# Revit family: Haworth_JiveTable_RoundBases
name_source: partatom
category: Furniture Systems
revit_build: Autodesk Revit 2018 (Build: 20170223_1515(x64)
units: mm (PartAtom-declared; Revit-internal decimal feet)

## family parameters
Always vertical = Yes
Cut with Voids When Loaded = No
OmniClass Number = 23.40.70.14.64.21
OmniClass Title = Systems Furniture
Part Type = Normal
Room Calculation Point = No
Round Connector Dimension = Use Diameter
Shared = No
Work Plane-Based = No

## types (33) — shared parameters
Assembly Code = E2020200
Custom Size = No
Manufacturer = Haworth, Inc.
Max. Depth Width = 30"
Max. Height = 42"
Min. Depth Width = 12"
Min. Height = 16"
Model = Haworth Jive
Revision Number = 0
Size = Verify Final Dim. w/ Haworth
Standard Depth Width = 24, 30, 36, 42, 48, 54, 60in.
Standard Heights = 16, 20, 29, 36, 42 in.
Table Thickness = 1 3/16"
URL = https://www.haworth.com
URL - Product = https://www.haworth.com
Warranty = http://www.haworth.com

## per-type parameters (varying)
| type | 4 6 8 Column | 4 Column | 4 Column 48d 48w | 4 Column Leg Distance | Actual Casters | Actual Depth | Actual Glides | Actual Height | Actual Table Depth | Bridge Base 48d 48w only | Casters | DW | Depth | Description | Glides | Height | Leg Height | X Base | X Base 2 3 Column | X Base 48d 48w only | X Base at 48d 48w |
| 30d 30w 29h - X Base - With Casters | No | No | No | 14" | Yes | 15" | No | 29" | 30" | No | Yes | 15" | 30" | Haworth Jive Table Round Bases - 30d 30w 29h - X Base - With Casters | No | 29" | 27 13/16" | Yes | Yes | Yes | No |
| 36d 36w 29h - X Base - With Casters | No | No | No | 14" | Yes | 18" | No | 29" | 36" | No | Yes | 18" | 36" | Haworth Jive Table Round Bases - 36d 36w 29h - X Base - With Casters | No | 29" | 27 13/16" | Yes | Yes | Yes | No |
| 42d 42w 29h - X Base - With Casters | No | No | No | 14" | Yes | 21" | No | 29" | 42" | No | Yes | 21" | 42" | Haworth Jive Table Round Bases - 42d 42w 29h - X Base - With Casters | No | 29" | 27 13/16" | Yes | Yes | Yes | No |
| 48d 48w 29h - X Base - With Casters | No | No | No | 14" | Yes | 24" | No | 29" | 48" | No | Yes | 24" | 48" | Haworth Jive Table Round Bases - 48d 48w 29h - X Base - With Casters | No | 29" | 27 13/16" | Yes | Yes | Yes | Yes |
| 30d 30w 42h - X Base - With Casters | No | No | No | 14" | Yes | 15" | No | 42" | 30" | No | Yes | 15" | 30" | Haworth Jive Table Round Bases - 30d 30w 42h - X Base - With Casters | No | 42" | 40 13/16" | Yes | Yes | Yes | No |
| 36d 36w 42h - X Base - With Casters | No | No | No | 14" | Yes | 18" | No | 42" | 36" | No | Yes | 18" | 36" | Haworth Jive Table Round Bases - 36d 36w 42h - X Base - With Casters | No | 42" | 40 13/16" | Yes | Yes | Yes | No |
| 42d 42w 42h - X Base - With Casters | No | No | No | 14" | Yes | 21" | No | 42" | 42" | No | Yes | 21" | 42" | Haworth Jive Table Round Bases - 42d 42w 42h - X Base - With Casters | No | 42" | 40 13/16" | Yes | Yes | Yes | No |
| 24d 24w 16h - X Base - With Glides | No | No | No | 14" | No | 12" | Yes | 16" | 24" | No | No | 12" | 24" | Haworth Jive Table Round Bases - 24d 24w 16h - X Base - With Glides | Yes | 16" | 14 13/16" | Yes | Yes | Yes | No |
| 30d 30w 16h - X Base - With Glides | No | No | No | 14" | No | 15" | Yes | 16" | 30" | No | No | 15" | 30" | Haworth Jive Table Round Bases - 30d 30w 16h - X Base - With Glides | Yes | 16" | 14 13/16" | Yes | Yes | Yes | No |
| 36d 36w 16h - X Base - With Glides | No | No | No | 14" | No | 18" | Yes | 16" | 36" | No | No | 18" | 36" | Haworth Jive Table Round Bases - 36d 36w 16h - X Base - With Glides | Yes | 16" | 14 13/16" | Yes | Yes | Yes | No |
| 42d 42w 16h - X Base - With Glides | No | No | No | 14" | No | 21" | Yes | 16" | 42" | No | No | 21" | 42" | Haworth Jive Table Round Bases - 42d 42w 16h - X Base - With Glides | Yes | 16" | 14 13/16" | Yes | Yes | Yes | No |
| 48d 48w 16h - X Base - With Glides | No | No | No | 14" | No | 24" | Yes | 16" | 48" | No | No | 24" | 48" | Haworth Jive Table Round Bases - 48d 48w 16h - X Base - With Glides | Yes | 16" | 14 13/16" | Yes | Yes | Yes | Yes |
| 24d 24w 20h - X Base - With Glides | No | No | No | 14" | No | 12" | Yes | 20" | 24" | No | No | 12" | 24" | Haworth Jive Table Round Bases - 24d 24w 20h - X Base - With Glides | Yes | 20" | 18 13/16" | Yes | Yes | Yes | No |
| 30d 30w 20h - X Base - With Glides | No | No | No | 14" | No | 15" | Yes | 20" | 30" | No | No | 15" | 30" | Haworth Jive Table Round Bases - 30d 30w 20h - X Base - With Glides | Yes | 20" | 18 13/16" | Yes | Yes | Yes | No |
| 36d 36w 20h - X Base - With Glides | No | No | No | 14" | No | 18" | Yes | 20" | 36" | No | No | 18" | 36" | Haworth Jive Table Round Bases - 36d 36w 20h - X Base - With Glides | Yes | 20" | 18 13/16" | Yes | Yes | Yes | No |
| 42d 42w 20h - X Base - With Glides | No | No | No | 14" | No | 21" | Yes | 20" | 42" | No | No | 21" | 42" | Haworth Jive Table Round Bases - 42d 42w 20h - X Base - With Glides | Yes | 20" | 18 13/16" | Yes | Yes | Yes | No |
| 48d 48w 20h - X Base - With Glides | No | No | No | 14" | No | 24" | Yes | 20" | 48" | No | No | 24" | 48" | Haworth Jive Table Round Bases - 48d 48w 20h - X Base - With Glides | Yes | 20" | 18 13/16" | Yes | Yes | Yes | Yes |
| 24d 24w 29h - X Base - With Glides | No | No | No | 14" | No | 12" | Yes | 29" | 24" | Yes | No | 12" | 24" | Haworth Jive Table Round Bases - 24d 24w 29h - X Base - With Glides | Yes | 29" | 27 13/16" | Yes | Yes | No | No |
| 30d 30w 29h - X Base - With Glides | No | No | No | 14" | No | 15" | Yes | 29" | 30" | Yes | No | 15" | 30" | Haworth Jive Table Round Bases - 30d 30w 29h - X Base - With Glides | Yes | 29" | 27 13/16" | Yes | Yes | No | No |
| 36d 36w 29h - X Base - With Glides | No | No | No | 14" | No | 18" | Yes | 29" | 36" | Yes | No | 18" | 36" | Haworth Jive Table Round Bases - 36d 36w 29h - X Base - With Glides | Yes | 29" | 27 13/16" | Yes | Yes | No | No |
| 42d 42w 29h - X Base - With Glides | No | No | No | 14" | No | 21" | Yes | 29" | 42" | Yes | No | 21" | 42" | Haworth Jive Table Round Bases - 42d 42w 29h - X Base - With Glides | Yes | 29" | 27 13/16" | Yes | Yes | No | No |
| 48d 48w 29h - X Base - With Glides | No | No | No | 14" | No | 24" | Yes | 29" | 48" | No | No | 24" | 48" | Haworth Jive Table Round Bases - 48d 48w 29h - X Base - With Glides | Yes | 29" | 27 13/16" | Yes | Yes | Yes | Yes |
| 30d 30w 36h - X Base - With Glides | No | No | No | 14" | No | 15" | Yes | 36" | 30" | No | No | 15" | 30" | Haworth Jive Table Round Bases - 30d 30w 36h - X Base - With Glides | Yes | 36" | 34 13/16" | Yes | Yes | Yes | No |
| 36d 36w 36h - X Base - With Glides | No | No | No | 14" | No | 18" | Yes | 36" | 36" | No | No | 18" | 36" | Haworth Jive Table Round Bases - 36d 36w 36h - X Base - With Glides | Yes | 36" | 34 13/16" | Yes | Yes | Yes | No |
| 42d 42w 36h - X Base - With Glides | No | No | No | 14" | No | 21" | Yes | 36" | 42" | No | No | 21" | 42" | Haworth Jive Table Round Bases - 42d 42w 36h - X Base - With Glides | Yes | 36" | 34 13/16" | Yes | Yes | Yes | No |
| 30d 30w 42h - X Base - With Glides | No | No | No | 14" | No | 15" | Yes | 42" | 30" | No | No | 15" | 30" | Haworth Jive Table Round Bases - 30d 30w 42h - X Base - With Glides | Yes | 42" | 40 13/16" | Yes | Yes | Yes | No |
| 36d 36w 42h - X Base - With Glides | No | No | No | 14" | No | 18" | Yes | 42" | 36" | No | No | 18" | 36" | Haworth Jive Table Round Bases - 36d 36w 42h - X Base - With Glides | Yes | 42" | 40 13/16" | Yes | Yes | Yes | No |
| 42d 42w 42h - X Base - With Glides | No | No | No | 14" | No | 21" | Yes | 42" | 42" | No | No | 21" | 42" | Haworth Jive Table Round Bases - 42d 42w 42h - X Base - With Glides | Yes | 42" | 40 13/16" | Yes | Yes | Yes | No |
| 54d 54w 20h - Bridge Base - With Glides | Yes | Yes | No | 16" | No | 27" | Yes | 20" | 54" | Yes | No | 27" | 54" | Haworth Jive Table Round Bases - 54d 54w 20h - Bridge Base - With Glides | Yes | 20" | 18 13/16" | No | No | No | No |
| 60d 60w 20h - Bridge Base - With Glides | Yes | Yes | No | 18" | No | 30" | Yes | 20" | 60" | Yes | No | 30" | 60" | Haworth Jive Table Round Bases - 60d 60w 20h - Bridge Base - With Glides | Yes | 20" | 18 13/16" | No | No | No | No |
| 48d 48w 29h - Bridge Base - With Glides | Yes | Yes | Yes | 14" | No | 24" | Yes | 29" | 48" | Yes | No | 24" | 48" | Haworth Jive Table Round Bases - 48d 48w 29h - Bridge Base - With Glides | Yes | 29" | 27 13/16" | No | No | No | No |
| 54d 54w 29h - Bridge Base - With Glides | Yes | Yes | No | 16" | No | 27" | Yes | 29" | 54" | Yes | No | 27" | 54" | Haworth Jive Table Round Bases - 54d 54w 29h - Bridge Base - With Glides | Yes | 29" | 27 13/16" | No | No | No | No |
| 60d 60w 29h - Bridge Base - With Glides | Yes | Yes | No | 18" | No | 30" | Yes | 29" | 60" | Yes | No | 30" | 60" | Haworth Jive Table Round Bases - 60d 60w 29h - Bridge Base - With Glides | Yes | 29" | 27 13/16" | No | No | No | No |

## geometry (parser evidence)
native form markers: Sweep x25
no freeform markers — native parametric forms only
